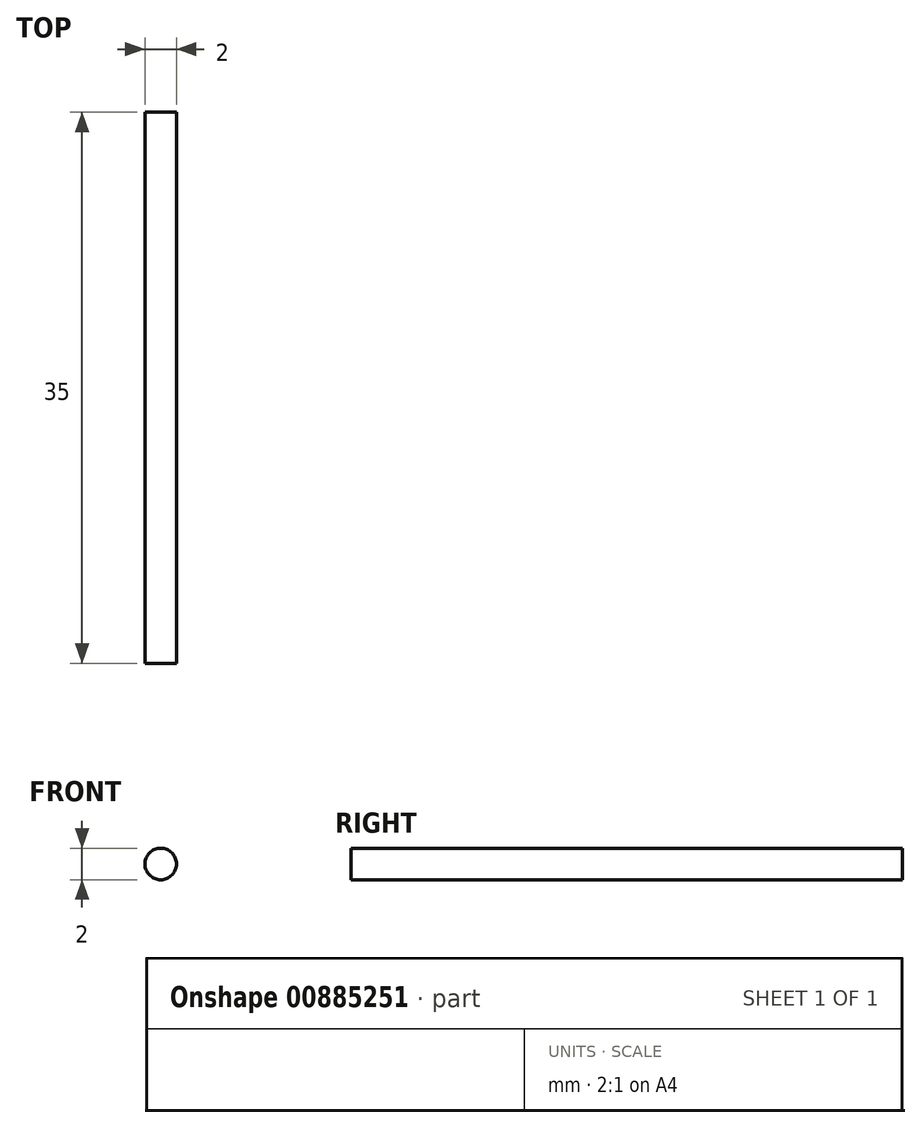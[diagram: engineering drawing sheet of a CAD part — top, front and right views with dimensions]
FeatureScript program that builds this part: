
annotation { "Feature Type Name" : "Feature", "Feature Type Description" : "" }
export const myFeature = defineFeature(function(context is Context, id is Id, definition is map)
    precondition{}
    {
        {
            var Q0;
            Q0=qCreatedBy(makeId("Front.planeOp"),FACE);
            var sketch = newSketch(context, id + "F0", { "sketchPlane" : qUnion([Q0])});
            skCircle(sketch, "E0", {"center": v(0, 0) * mm, "radius": 1 * mm});
            skSolve(sketch);
        }
        {
            var Q0;
            Q0=makeQuery(id+"F0.imprint","IMPRINT",FACE,{"disambiguationData":[TD([[makeQuery(id+"F0.imprint","IMPRINT",EDGE,{"derivedFrom":sQuery(id+"F0.wireOp",EDGE,"E0")}),1.0]])]});
            extrude(context, id + "F1", {"entities" : qUnion([Q0]), "depth" : 35 * mm, "offsetDistance" : 25 * mm});
        }
    });
